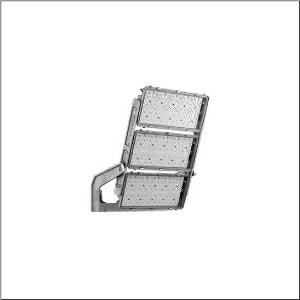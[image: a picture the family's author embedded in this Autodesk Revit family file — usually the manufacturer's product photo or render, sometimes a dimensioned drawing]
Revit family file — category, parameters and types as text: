
# Revit family: floodlight_fl_11_maxi_pro_remote___pl43_5xa779524a01aa_32ee
name_source: partatom
category: Lighting Fixtures
units: mm (PartAtom-declared; Revit-internal decimal feet)

## family parameters
Cut with Voids When Loaded = No
Host = Face
Light Source = No
Part Type = Normal
Room Calculation Point = No
Round Connector Dimension = Use Diameter
Shared = No

## types (1)
- --- (1 x LED, 130000 lm, 1334.7 W, 5700K)
    Apparent Load = 1335 VA
    CIE Flux Codes = 25 74 99 100 100
    Color Rendering = 90
    Color Temperature = 5700K
    Default Elevation = 1800 mm
    Description = Floodlight FL 11  maxi  pro Remote floodlight; light control with lens of PMMA; cover panel of toughened safety glass, transparent; light distribution: PL43, asymmetric direct distribution, LEDcolour temperature: 5700K, rated luminous flux: 130.000lm, colour rendering: CRI > 90, light colour: 957; luminous efficacy: 97lm/W; brightness control: DMX+RDM; with terminal, 8-pole, max. 2.5mm², mains connection: 220..240V/380..400V AC, 50/60Hz, surge voltage resistance: line to ground: 10kV, ECG replaceable separately, no afterglow with DALI off / DMX off command, LED unit replaceable without ESD environment, dustproof LED module, dimming range 10..100%; 1335W floodlight with 3x LED unit of diecast aluminium, coated grey; length: 713mm / width: 651mm / height: 338mm; mounting bracket, of diecast aluminium, uncoated, natural, equipment: Power, protection rating (complete): IP66; insulation class (complete): insulation class I (protective earthing); certification: CE, ENEC, VDE; ball protection: ball impact resistance with accessories, impact resistance: IK07; only for outdoor installations, rated ambient temperature 10°C, permissible operating ambient temperature: -40..+30°C, permissible storage temperature: -40..+85°Cpackaging unit: 1 piece

Light Distribution: PL43
    Height = 320 mm
    Lamp = 1 x LED
    Lamp Light Flux = 130000 lm
    Lamp Power = 1334.7 W
    Lamp count = 1
    Length = 1002 mm
    Luminous efficacy = 97 lm/W
    Manufacturer = Siteco
    ModVariant = No
    Model = 5XA779524A01AA
    Mounting Place = Ceiling
    Mounting Type = Surface mounted
    Number of Poles = 1
    OnlyDefault = Yes
    Power Factor = 1
    Product Name = Floodlight FL 11 maxi pro Remote | PL43
    Product group = floodlight | ceiling mounted
    ProductGroupID = 301
    Protection Class = Protection class I
    Protection Degree = IP 66
    RLX_Detail_Level = 1
    RLX_Emergency_Light_Flux = 0 lm
    RLX_Emergency_Type = 0
    RLX_Emergency_Type_DB = No
    RlxData = <blob elided: 52381 chars, md5=452355a4>
    Socket = socket
    Standby Power = 0 W
    System Light Flux = 130000 lm
    System Power = 1335 W
    Type Comments = factory setting: luminous flux: 100 % | dim-lin: 255 | 920 mA
    Type Image = l_1349141.jpg
    URL = http://relux.com
    VarID = @adj_096596
    Voltage = 0 V
    Weight = 0.00 kg
    Width = 655 mm

## geometry (parser evidence)
native form markers: Blend x4, Sweep x13
no freeform markers — native parametric forms only
